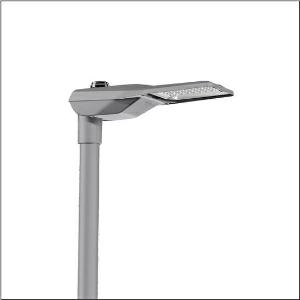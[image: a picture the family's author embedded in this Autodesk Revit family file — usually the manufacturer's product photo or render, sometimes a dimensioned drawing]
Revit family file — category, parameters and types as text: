
# Revit family: streetlight_sl_21_mini___stw1_0a_5xe6e37n08gb_9d35
name_source: partatom
category: Lighting Fixtures
units: mm (PartAtom-declared; Revit-internal decimal feet)

## family parameters
Cut with Voids When Loaded = No
Host = Face
Light Source = No
Part Type = Normal
Room Calculation Point = No
Round Connector Dimension = Use Diameter
Shared = No

## types (1)
- --- (1 x LED, 5940 lm, 40.4 W, 3000K)
    Apparent Load = 40 VA
    CIE Flux Codes = 38 75 98 100 100
    Color Rendering = 70
    Color Temperature = 3000K
    Default Elevation = 1800 mm
    Description = Streetlight SL 21 mini, mast luminaire, primary light control with lens, of PMMA, primary optical cover: cover, of toughened safety glass, transparent, light distribution: STW1.0a, light emission: direct distribution, primary light characteristic: asymmetric, installation type: side-entry, LED, 3G 1.5mm², High Power LED, rated luminous flux: 5.940lm, luminous efficacy: 147lm/W, light colour: 730, colour temperature: 3000K, control: overheat protection, pre-setting: linear dimming characteristic, constant luminous flux control, time-dependent luminous flux control, flexible luminous flux parameterisation, mains connection: 230..240V, AC, 50/60Hz, connection cable pre-assembled, cable length: 8,5m, wiring characteristics: H07RN-F, start of lifetime: 40W, end of service life: 41W, reduction: 19W, luminaire housing, of diecast aluminium (EN AC-44300), powder-coated, Siteco® metallic grey (DB 702S), corrosivity category C5 mid according to DIN EN ISO 12944, multi-level sealing system, sealing non-destructively replaceable, inclination adjustable: 0°, 5°, 10°, 15°, length: 628mm, width: 235mm, height: 110mm, spigot size: 42mm (side-entry), protection rating (complete): IP66, insulation class (complete): insulation class I (protective earthing), certification: CE, ENEC, ENEC+, VDE, impact resistance: IK09, permissible operating ambient temperature for outdoor applications: -40..+50°C, standard-compliant lighting for roads and squares, packaging unit: 1 piece

Light Distribution: STW1.0a
    Height = 110 mm
    Lamp = 1 x LED
    Lamp Light Flux = 5940 lm
    Lamp Power = 40.4 W
    Lamp count = 1
    Length = 625 mm
    Luminous efficacy = 147 lm/W
    Manufacturer = Siteco
    ModVariant = No
    Model = 5XE6E37N08GB
    Number of Poles = 1
    OnlyDefault = Yes
    Power Factor = 1
    Product Name = Streetlight SL 21 mini | STW1.0a
    Product group = mast luminaire | pylon top
    ProductGroupID = 6100
    Protection Class = Protection class I
    Protection Degree = IP 66
    RLX_Detail_Level = 1
    RLX_Emergency_Light_Flux = 0 lm
    RLX_Emergency_Type = 0
    RLX_Emergency_Type_DB = No
    RlxData = <blob elided: 91717 chars, md5=8fadfa9c>
    Socket = socket
    Standby Power = 0 W
    System Light Flux = 5940 lm
    System Power = 40 W
    Type Comments = factory setting: luminous flux: 100 % | dim-lin: 254 | 812 mA
    Type Image = l_1294379.jpg
    URL = http://relux.com
    VarID = @adj_105519
    Voltage = 0 V
    Weight = 0.00 kg
    Width = 234 mm

## geometry (parser evidence)
native form markers: Blend x4, Sweep x11
no freeform markers — native parametric forms only
